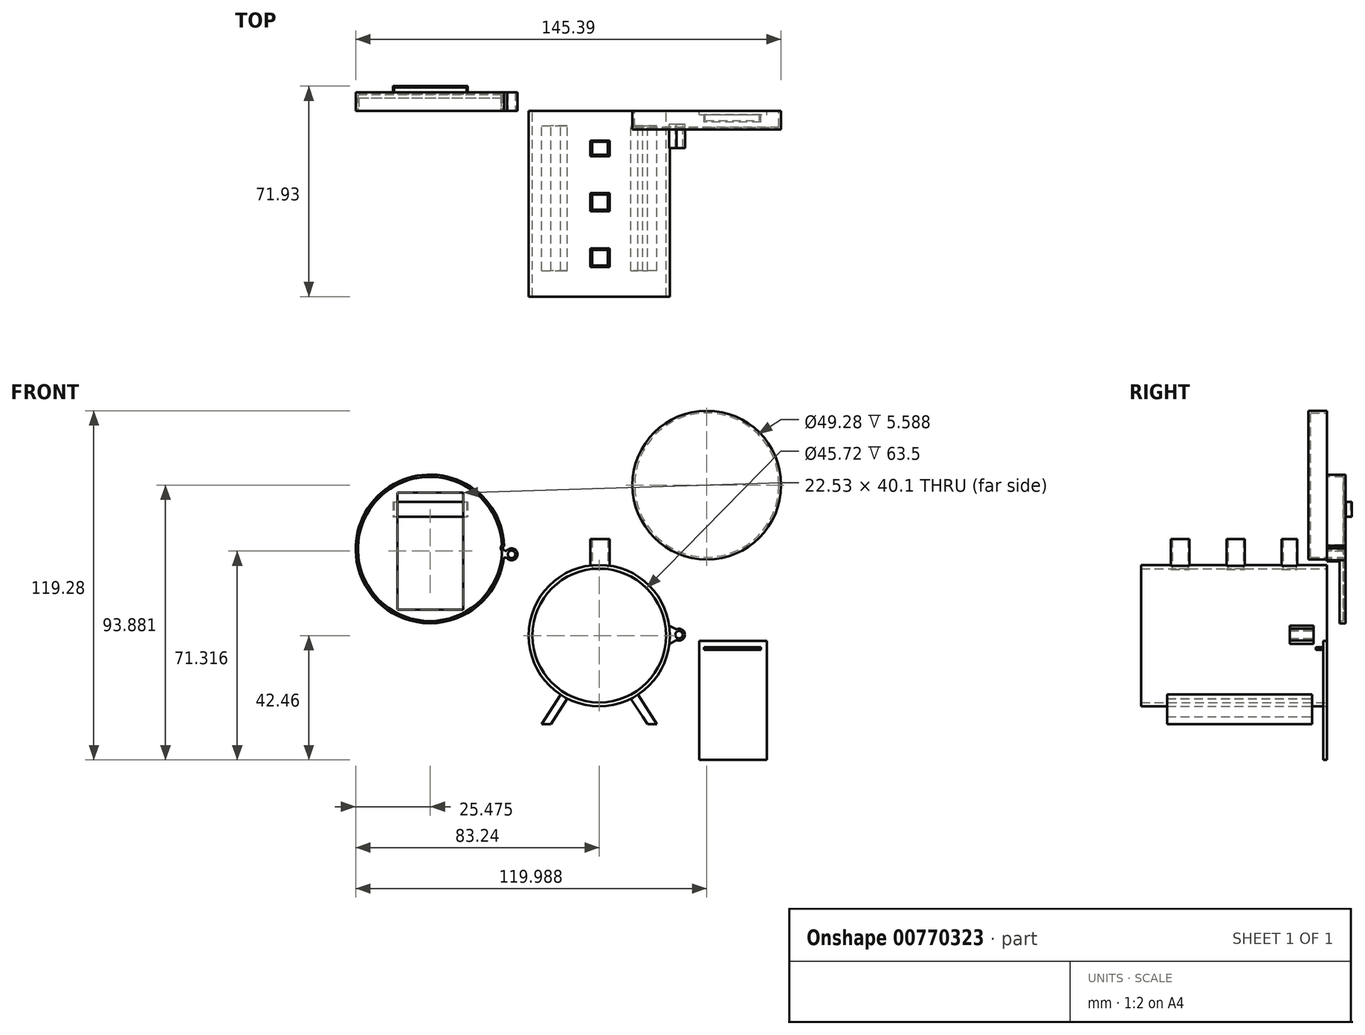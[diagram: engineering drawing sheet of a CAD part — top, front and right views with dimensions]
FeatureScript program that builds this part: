
annotation { "Feature Type Name" : "Feature", "Feature Type Description" : "" }
export const myFeature = defineFeature(function(context is Context, id is Id, definition is map)
    precondition{}
    {
        {
            var Q0;
            Q0=qCreatedBy(makeId("Front.planeOp"),FACE);
            var sketch = newSketch(context, id + "F0", { "sketchPlane" : qUnion([Q0])});
            skCircle(sketch, "E0", {"center": v(-57.84, 29.6) * mm, "radius": 25.4 * mm});
            skCircle(sketch, "E1", {"center": v(36.75, 51.42) * mm, "radius": 25.4 * mm});
            skCircle(sketch, "E2", {"center": v(0, 0) * mm, "radius": 24.13 * mm});
            skCircle(sketch, "E3", {"center": v(0, 0) * mm, "radius": 22.86 * mm});
            skCircle(sketch, "E4", {"center": v(-29.97, 27.74) * mm, "radius": 2.03 * mm});
            skCircle(sketch, "E5", {"center": v(-29.97, 27.74) * mm, "radius": 1.27 * mm});
            skPoint(sketch, "E6", {"position": v(-82.6, 23.93) * mm});
            skArc(sketch, "E7", {"start": v(-31.32, 26.22) * mm, "mid": v(-31.92, 26.64) * mm, "end": v(-32.63, 26.47) * mm});
            skArc(sketch, "E8", {"start": v(-32.46, 30.66) * mm, "mid": v(-32.74, 29.38) * mm, "end": v(-31.47, 29.1) * mm});
            skCircle(sketch, "E9", {"center": v(27.24, 0.29) * mm, "radius": 2.03 * mm});
            skCircle(sketch, "E10", {"center": v(27.24, 0.29) * mm, "radius": 1.27 * mm});
            skLineSegment(sketch, "E11", {"start": v(26.39, 2.13) * mm, "end": v(23.9, 3.39) * mm});
            skLineSegment(sketch, "E12", {"start": v(26.41, -1.57) * mm, "end": v(23.96, -2.9) * mm});
            skLineSegment(sketch, "E13", {"start": v(-19.67, -30.34) * mm, "end": v(-13.17, -20.22) * mm});
            skLineSegment(sketch, "E14", {"start": v(19.68, -30.34) * mm, "end": v(13.24, -20.17) * mm});
            skLineSegment(sketch, "E15", {"start": v(-14.86, -27.7) * mm, "end": v(-10.97, -21.5) * mm});
            skLineSegment(sketch, "E16", {"start": v(14.87, -27.7) * mm, "end": v(10.75, -21.6) * mm});
            skLineSegment(sketch, "E17", {"start": v(14.87, -27.7) * mm, "end": v(16.46, -30.34) * mm});
            skLineSegment(sketch, "E18", {"start": v(19.68, -30.34) * mm, "end": v(16.46, -30.34) * mm});
            skLineSegment(sketch, "E19", {"start": v(-14.86, -27.7) * mm, "end": v(-16.51, -30.34) * mm});
            skLineSegment(sketch, "E20", {"start": v(-19.67, -30.34) * mm, "end": v(-16.51, -30.34) * mm});
            skSolve(sketch);
        }
        {
            var Q0;
            Q0=qCreatedBy(makeId("Top.planeOp"),FACE);
            var sketch = newSketch(context, id + "F1", { "sketchPlane" : qUnion([Q0])});
            skLineSegment(sketch, "E21.bottom", {"start": v(-84.43, -2.05) * mm, "end": v(-31.1, -2.05) * mm});
            skLineSegment(sketch, "E21.top", {"start": v(-84.43, 4.3) * mm, "end": v(-31.1, 4.3) * mm});
            skLineSegment(sketch, "E21.left", {"start": v(-84.43, -2.05) * mm, "end": v(-84.43, 4.3) * mm});
            skLineSegment(sketch, "E21.right", {"start": v(-31.1, -2.05) * mm, "end": v(-31.1, 4.3) * mm});
            skLineSegment(sketch, "E22", {"start": v(-70.15, 8.43) * mm, "end": v(-45.37, 8.43) * mm});
            skLineSegment(sketch, "E23", {"start": v(-70.15, 8) * mm, "end": v(-45.37, 8) * mm});
            skLineSegment(sketch, "E24.bottom", {"start": v(-70.15, 8.43) * mm, "end": v(-70.53, 8.43) * mm});
            skLineSegment(sketch, "E24.right", {"start": v(-70.53, 8.43) * mm, "end": v(-70.53, 6.4) * mm});
            skLineSegment(sketch, "E25", {"start": v(-45.37, 6.4) * mm, "end": v(-45.37, 8) * mm});
            skLineSegment(sketch, "E26", {"start": v(-44.98, 6.4) * mm, "end": v(-44.98, 8.43) * mm});
            skLineSegment(sketch, "E27", {"start": v(-44.98, 8.43) * mm, "end": v(-45.37, 8.43) * mm});
            skLineSegment(sketch, "E28", {"start": v(-70.15, 8) * mm, "end": v(-70.15, 6.4) * mm});
            skLineSegment(sketch, "E29", {"start": v(-70.53, 6.4) * mm, "end": v(-70.15, 6.4) * mm});
            skLineSegment(sketch, "E30", {"start": v(-45.37, 6.4) * mm, "end": v(-44.98, 6.4) * mm});
            skSolve(sketch);
        }
        {
            var Q0;
            Q0=qCreatedBy(makeId("Front.planeOp"),FACE);
            var sketch = newSketch(context, id + "F2", { "sketchPlane" : qUnion([Q0])});
            skLineSegment(sketch, "E31.bottom", {"start": v(-46.5, 48.9) * mm, "end": v(-69.03, 48.9) * mm});
            skLineSegment(sketch, "E31.top", {"start": v(-46.5, 8.8) * mm, "end": v(-69.03, 8.8) * mm});
            skLineSegment(sketch, "E31.left", {"start": v(-46.5, 48.9) * mm, "end": v(-46.5, 8.8) * mm});
            skLineSegment(sketch, "E31.right", {"start": v(-69.03, 48.9) * mm, "end": v(-69.03, 8.8) * mm});
            skLineSegment(sketch, "E32.bottom", {"start": v(34.2, -42.46) * mm, "end": v(57.24, -42.46) * mm});
            skLineSegment(sketch, "E32.top", {"start": v(34.2, -1.82) * mm, "end": v(57.24, -1.82) * mm});
            skLineSegment(sketch, "E32.left", {"start": v(34.2, -42.46) * mm, "end": v(34.2, -1.82) * mm});
            skLineSegment(sketch, "E32.right", {"start": v(57.24, -42.46) * mm, "end": v(57.24, -1.82) * mm});
            skLineSegment(sketch, "E33.bottom", {"start": v(55.19, -3.96) * mm, "end": v(35.8, -3.96) * mm});
            skLineSegment(sketch, "E33.top", {"start": v(55.19, -4.91) * mm, "end": v(35.8, -4.91) * mm});
            skLineSegment(sketch, "E33.left", {"start": v(55.19, -3.96) * mm, "end": v(55.19, -4.91) * mm});
            skLineSegment(sketch, "E33.right", {"start": v(35.8, -3.96) * mm, "end": v(35.8, -4.91) * mm});
            skSolve(sketch);
        }
        {
            var Q0;
            Q0=makeQuery(id+"F0.imprint","IMPRINT",FACE,{"disambiguationData":[TD([[makeQuery(id+"F0.imprint","IMPRINT",EDGE,{"derivedFrom":sQuery(id+"F0.wireOp",EDGE,"E0")}),1.0]])]});
            var Q1;
            Q1=makeQuery(id+"F0.imprint","IMPRINT",FACE,{"disambiguationData":[TD([[makeQuery(id+"F0.imprint","IMPRINT",EDGE,{"derivedFrom":sQuery(id+"F0.wireOp",EDGE,"C6JpCIsN-Ug02-e6we-Fdyt-q6CA1btcc4Vs")}),1.0]])]});
            var Q2;
            Q2=sQuery(id+"F0.wireOp",EDGE,"E0");
            extrude(context, id + "F3", {"entities" : qUnion([Q0, Q1]), "surfaceEntities" : qUnion([Q2]), "oppositeDirection" : true, "depth" : 6.35 * mm, "offsetDistance" : 25.4 * mm});
        }
        {
            var Q0;
            Q0=makeQuery(id+"F0.imprint","IMPRINT",FACE,{"disambiguationData":[TD([[makeQuery(id+"F0.imprint","IMPRINT",EDGE,{"derivedFrom":sQuery(id+"F0.wireOp",EDGE,"E1")}),1.0]])]});
            var Q1;
            Q1=sQuery(id+"F0.wireOp",EDGE,"E1");
            extrude(context, id + "F4", {"entities" : qUnion([Q0]), "surfaceEntities" : qUnion([Q1]), "depth" : 6.35 * mm, "offsetDistance" : 25.4 * mm});
        }
        {
            var Q0;
            Q0=makeQuery(id+"F0.imprint","IMPRINT",FACE,{"disambiguationData":[TD([[makeQuery(id+"F0.imprint","IMPRINT",EDGE,{"derivedFrom":sQuery(id+"F0.wireOp",EDGE,"E2")}),1.0]])]});
            var Q1;
            Q1=sQuery(id+"F0.wireOp",EDGE,"E2");
            extrude(context, id + "F5", {"entities" : qUnion([Q0]), "surfaceEntities" : qUnion([Q1]), "depth" : 63.5 * mm, "offsetDistance" : 25.4 * mm});
        }
        {
            var Q0;
            Q0=makeQuery(id+"F0.imprint","IMPRINT",FACE,{"disambiguationData":[TD([[makeQuery(id+"F0.imprint","IMPRINT",EDGE,{"derivedFrom":sQuery(id+"F0.wireOp",EDGE,"E9")}),1.0]])]});
            var Q1;
            {var subQ0=sQuery(id+"F0.wireOp",EDGE,"4RHoPJRj-vLUF-sawJ-OMLI-LrxcrPkEBD53");Q1=makeQuery(id+"F0.imprint","IMPRINT",FACE,{"disambiguationData":[TD([[makeQuery(id+"F0.imprint","IMPRINT",EDGE,{"derivedFrom":subQ0}),-1.0]])]});}
            var Q2;
            {var subQ0=sQuery(id+"F0.wireOp",EDGE,"GAmkWysi-UypD-Y6Y5-O07L-UFwPJowarkKv");Q2=makeQuery(id+"F0.imprint","IMPRINT",FACE,{"disambiguationData":[TD([[makeQuery(id+"F0.imprint","IMPRINT",EDGE,{"derivedFrom":subQ0}),-1.0]])]});}
            var Q3;
            {var subQ0=sQuery(id+"F0.wireOp",EDGE,"E11");Q3=makeQuery(id+"F0.imprint","IMPRINT",FACE,{"disambiguationData":[TD([[makeQuery(id+"F0.imprint","IMPRINT",EDGE,{"derivedFrom":subQ0}),1.0]])]});}
            extrude(context, id + "F6", {"entities" : qUnion([Q0, Q1, Q2, Q3]), "depth" : 12.7 * mm, "offsetDistance" : 25.4 * mm});
        }
        {
            var Q0;
            Q0=makeQuery(id+"F3.opExtrude","CAP_FACE",FACE,{"disambiguationData":[OSD([sQuery(id+"F0.wireOp",EDGE,"E0")])],"isStart":true});
            shell(context, id + "F7", {"entities" : qUnion([Q0]), "thickness" : 0.76 * mm});
        }
        {
            var Q0;
            Q0=makeQuery(id+"F1.imprint","IMPRINT",FACE,{"disambiguationData":[TD([[makeQuery(id+"F1.imprint","IMPRINT",EDGE,{"derivedFrom":sQuery(id+"F1.wireOp",EDGE,"E21.bottom")}),1.0]])]});
            extrude(context, id + "F8", {"entities" : qUnion([Q0]), "operationType" : NewBodyOperationType.REMOVE, "depth" : 25.4 * mm, "offsetDistance" : 25.4 * mm});
        }
        {
            var Q0;
            {var subQ0=sQuery(id+"F0.wireOp",EDGE,"E7");var subQ1=sQuery(id+"F0.wireOp",EDGE,"E0");var subQ2=makeQuery(id+"F0.imprint","INTERSECT",VERTEX,{"derivedFrom":[subQ1,subQ0]});Q0=makeQuery(id+"F0.imprint","IMPRINT",FACE,{"disambiguationData":[TD([[makeQuery(id+"F0.imprint","IMPRINT",EDGE,{"disambiguationData":[TD([[subQ2,-1.0]])],"derivedFrom":subQ1}),-1.0]])]});}
            var Q1;
            Q1=makeQuery(id+"F0.imprint","IMPRINT",FACE,{"disambiguationData":[TD([[makeQuery(id+"F0.imprint","IMPRINT",EDGE,{"derivedFrom":sQuery(id+"F0.wireOp",EDGE,"E5")}),-1.0]])]});
            var Q2;
            Q2=sQuery(id+"F0.wireOp",EDGE,"E4");
            var Q3;
            Q3=sQuery(id+"F0.wireOp",EDGE,"uoLiYAiw-HX8z-VXfl-kdci-X3IbJ3UhpFK8");
            extrude(context, id + "F9", {"entities" : qUnion([Q0, Q1]), "operationType" : NewBodyOperationType.ADD, "surfaceEntities" : qUnion([Q2, Q3]), "oppositeDirection" : true, "depth" : 6.35 * mm, "offsetDistance" : 25.4 * mm});
        }
        {
            var Q0;
            Q0=makeQuery(id+"F4.opExtrude","CAP_FACE",FACE,{"disambiguationData":[OSD([sQuery(id+"F0.wireOp",EDGE,"E1")])],"isStart":true});
            shell(context, id + "F10", {"entities" : qUnion([Q0]), "thickness" : 0.76 * mm});
        }
        {
            var Q0;
            Q0=makeQuery(id+"F2.imprint","IMPRINT",FACE,{"disambiguationData":[TD([[makeQuery(id+"F2.imprint","IMPRINT",EDGE,{"derivedFrom":sQuery(id+"F2.wireOp",EDGE,"E31.bottom")}),1.0]])]});
            extrude(context, id + "F11", {"entities" : qUnion([Q0]), "operationType" : NewBodyOperationType.REMOVE, "surfaceOperationType" : NewSurfaceOperationType.ADD, "oppositeDirection" : true, "depth" : 12.7 * mm, "offsetDistance" : 25.4 * mm});
        }
        {
            var Q0;
            Q0=makeQuery(id+"F0.imprint","IMPRINT",FACE,{"disambiguationData":[TD([[makeQuery(id+"F0.imprint","IMPRINT",EDGE,{"derivedFrom":sQuery(id+"F0.wireOp",EDGE,"E10")}),-1.0]])]});
            var Q1;
            {var subQ0=sQuery(id+"F0.wireOp",EDGE,"E11");Q1=makeQuery(id+"F0.imprint","IMPRINT",FACE,{"disambiguationData":[TD([[makeQuery(id+"F0.imprint","IMPRINT",EDGE,{"derivedFrom":subQ0}),1.0]])]});}
            extrude(context, id + "F12", {"entities" : qUnion([Q0, Q1]), "operationType" : NewBodyOperationType.REMOVE, "depth" : 4.57 * mm, "offsetDistance" : 25.4 * mm});
        }
        {
            var Q0;
            Q0=makeQuery(id+"F1.imprint","IMPRINT",FACE,{"disambiguationData":[TD([[makeQuery(id+"F1.imprint","IMPRINT",EDGE,{"derivedFrom":sQuery(id+"F1.wireOp",EDGE,"E22")}),-1.0]])]});
            var Q1;
            Q1=sQuery(id+"F1.wireOp",EDGE,"E23");
            var Q2;
            Q2=sQuery(id+"F1.wireOp",EDGE,"E22");
            var Q3;
            Q3=sQuery(id+"F1.wireOp",EDGE,"E24.right");
            var Q4;
            Q4=sQuery(id+"F1.wireOp",EDGE,"E28");
            var Q5;
            Q5=sQuery(id+"F1.wireOp",EDGE,"E26");
            var Q6;
            Q6=sQuery(id+"F1.wireOp",EDGE,"E25");
            var Q7;
            Q7=sQuery(id+"F1.wireOp",EDGE,"E27");
            var Q8;
            Q8=sQuery(id+"F1.wireOp",EDGE,"E24.top");
            var Q9;
            Q9=sQuery(id+"F1.wireOp",EDGE,"XSHV3Paq-2D3R-pDyN-Gvgj-U2klOx5jiF1c");
            var Q10;
            Q10=sQuery(id+"F1.wireOp",EDGE,"E24.bottom");
            extrude(context, id + "F13", {"entities" : qUnion([Q0]), "operationType" : NewBodyOperationType.ADD, "surfaceEntities" : qUnion([Q1, Q2, Q3, Q4, Q5, Q6, Q7, Q8, Q9, Q10]), "depth" : 45.72 * mm, "offsetDistance" : 25.4 * mm});
        }
        {
            var Q0;
            Q0=makeQuery(id+"F1.imprint","IMPRINT",FACE,{"disambiguationData":[TD([[makeQuery(id+"F1.imprint","IMPRINT",EDGE,{"derivedFrom":sQuery(id+"F1.wireOp",EDGE,"E22")}),-1.0]])]});
            var Q1;
            Q1=sQuery(id+"F1.wireOp",EDGE,"E28");
            var Q2;
            Q2=sQuery(id+"F1.wireOp",EDGE,"E23");
            var Q3;
            Q3=sQuery(id+"F1.wireOp",EDGE,"E25");
            var Q4;
            Q4=sQuery(id+"F1.wireOp",EDGE,"E26");
            var Q5;
            Q5=sQuery(id+"F1.wireOp",EDGE,"E24.right");
            var Q6;
            Q6=sQuery(id+"F1.wireOp",EDGE,"E22");
            var Q7;
            Q7=sQuery(id+"F1.wireOp",EDGE,"E27");
            var Q8;
            Q8=sQuery(id+"F1.wireOp",EDGE,"E24.top");
            var Q9;
            Q9=sQuery(id+"F1.wireOp",EDGE,"XSHV3Paq-2D3R-pDyN-Gvgj-U2klOx5jiF1c");
            var Q10;
            Q10=sQuery(id+"F1.wireOp",EDGE,"E24.bottom");
            extrude(context, id + "F14", {"entities" : qUnion([Q0]), "operationType" : NewBodyOperationType.REMOVE, "surfaceEntities" : qUnion([Q1, Q2, Q3, Q4, Q5, Q6, Q7, Q8, Q9, Q10]), "depth" : 40.64 * mm, "offsetDistance" : 25.4 * mm});
        }
        {
            var Q0;
            Q0=makeQuery(id+"F2.imprint","IMPRINT",FACE,{"disambiguationData":[TD([[makeQuery(id+"F2.imprint","IMPRINT",EDGE,{"derivedFrom":sQuery(id+"F2.wireOp",EDGE,"E32.bottom")}),1.0]])]});
            extrude(context, id + "F15", {"entities" : qUnion([Q0]), "depth" : 1.27 * mm, "offsetDistance" : 25.4 * mm});
        }
        {
            var Q0;
            Q0=qCreatedBy(makeId("Top.planeOp"),FACE);
            var sketch = newSketch(context, id + "F16", { "sketchPlane" : qUnion([Q0])});
            skLineSegment(sketch, "E34.bottom", {"start": v(-3, -10.16) * mm, "end": v(3.54, -10.16) * mm});
            skLineSegment(sketch, "E34.top", {"start": v(-3, -15.53) * mm, "end": v(3.54, -15.53) * mm});
            skLineSegment(sketch, "E34.left", {"start": v(-3, -10.16) * mm, "end": v(-3, -15.53) * mm});
            skLineSegment(sketch, "E34.right", {"start": v(3.54, -10.16) * mm, "end": v(3.54, -15.53) * mm});
            skLineSegment(sketch, "E35.bottom", {"start": v(-3, -28.07) * mm, "end": v(3.54, -28.07) * mm});
            skLineSegment(sketch, "E35.top", {"start": v(-3, -34.35) * mm, "end": v(3.54, -34.35) * mm});
            skLineSegment(sketch, "E35.left", {"start": v(-3, -28.07) * mm, "end": v(-3, -34.35) * mm});
            skLineSegment(sketch, "E35.right", {"start": v(3.54, -28.07) * mm, "end": v(3.54, -34.35) * mm});
            skLineSegment(sketch, "E36.bottom", {"start": v(-3, -47.05) * mm, "end": v(3.54, -47.05) * mm});
            skLineSegment(sketch, "E36.top", {"start": v(-3, -53.34) * mm, "end": v(3.54, -53.34) * mm});
            skLineSegment(sketch, "E36.left", {"start": v(-3, -47.05) * mm, "end": v(-3, -53.34) * mm});
            skLineSegment(sketch, "E36.right", {"start": v(3.54, -47.05) * mm, "end": v(3.54, -53.34) * mm});
            skLineSegment(sketch, "E37.bottom", {"start": v(-2.43, -10.6) * mm, "end": v(2.96, -10.6) * mm});
            skLineSegment(sketch, "E37.top", {"start": v(-2.43, -14.99) * mm, "end": v(2.96, -14.99) * mm});
            skLineSegment(sketch, "E37.left", {"start": v(-2.43, -10.6) * mm, "end": v(-2.43, -14.99) * mm});
            skLineSegment(sketch, "E37.right", {"start": v(2.96, -10.6) * mm, "end": v(2.96, -14.99) * mm});
            skLineSegment(sketch, "E38.bottom", {"start": v(-2.44, -28.57) * mm, "end": v(2.96, -28.57) * mm});
            skLineSegment(sketch, "E38.top", {"start": v(-2.44, -33.77) * mm, "end": v(2.96, -33.77) * mm});
            skLineSegment(sketch, "E38.left", {"start": v(-2.44, -28.57) * mm, "end": v(-2.44, -33.77) * mm});
            skLineSegment(sketch, "E38.right", {"start": v(2.96, -28.57) * mm, "end": v(2.96, -33.77) * mm});
            skLineSegment(sketch, "E39.bottom", {"start": v(-2.44, -47.57) * mm, "end": v(2.96, -47.57) * mm});
            skLineSegment(sketch, "E39.top", {"start": v(-2.44, -52.83) * mm, "end": v(2.96, -52.83) * mm});
            skLineSegment(sketch, "E39.left", {"start": v(-2.44, -47.57) * mm, "end": v(-2.44, -52.83) * mm});
            skLineSegment(sketch, "E39.right", {"start": v(2.96, -47.57) * mm, "end": v(2.96, -52.83) * mm});
            skSolve(sketch);
        }
        {
            var Q0;
            Q0 = qSketchRegion(id + "F16", true);
            extrude(context, id + "F17", {"entities" : qUnion([Q0]), "operationType" : NewBodyOperationType.ADD, "depth" : 33.02 * mm, "offsetDistance" : 25.4 * mm});
        }
        {
            var Q0;
            Q0=makeQuery(id+"F16.imprint","IMPRINT",FACE,{"disambiguationData":[TD([[makeQuery(id+"F16.imprint","IMPRINT",EDGE,{"derivedFrom":sQuery(id+"F16.wireOp",EDGE,"E35.bottom")}),-1.0]])]});
            var Q1;
            Q1=makeQuery(id+"F16.imprint","IMPRINT",FACE,{"disambiguationData":[TD([[makeQuery(id+"F16.imprint","IMPRINT",EDGE,{"derivedFrom":sQuery(id+"F16.wireOp",EDGE,"E34.bottom")}),-1.0]])]});
            var Q2;
            Q2=makeQuery(id+"F16.imprint","IMPRINT",FACE,{"disambiguationData":[TD([[makeQuery(id+"F16.imprint","IMPRINT",EDGE,{"derivedFrom":sQuery(id+"F16.wireOp",EDGE,"E36.bottom")}),-1.0]])]});
            extrude(context, id + "F18", {"entities" : qUnion([Q0, Q1, Q2]), "operationType" : NewBodyOperationType.REMOVE, "depth" : 22.86 * mm, "offsetDistance" : 25.4 * mm});
        }
        {
            var Q0;
            Q0=makeQuery(id+"F16.imprint","IMPRINT",FACE,{"disambiguationData":[TD([[makeQuery(id+"F16.imprint","IMPRINT",EDGE,{"derivedFrom":sQuery(id+"F16.wireOp",EDGE,"E37.bottom")}),-1.0]])]});
            var Q1;
            Q1=makeQuery(id+"F16.imprint","IMPRINT",FACE,{"disambiguationData":[TD([[makeQuery(id+"F16.imprint","IMPRINT",EDGE,{"derivedFrom":sQuery(id+"F16.wireOp",EDGE,"E38.bottom")}),-1.0]])]});
            var Q2;
            Q2=makeQuery(id+"F16.imprint","IMPRINT",FACE,{"disambiguationData":[TD([[makeQuery(id+"F16.imprint","IMPRINT",EDGE,{"derivedFrom":sQuery(id+"F16.wireOp",EDGE,"E39.bottom")}),-1.0]])]});
            var Q3;
            Q3=sQuery(id+"F16.wireOp",EDGE,"E37.left");
            var Q4;
            Q4=sQuery(id+"F16.wireOp",EDGE,"E37.right");
            var Q5;
            Q5=sQuery(id+"F16.wireOp",EDGE,"E37.bottom");
            var Q6;
            Q6=sQuery(id+"F16.wireOp",EDGE,"E37.top");
            var Q7;
            Q7=sQuery(id+"F16.wireOp",EDGE,"E38.bottom");
            var Q8;
            Q8=sQuery(id+"F16.wireOp",EDGE,"E38.top");
            var Q9;
            Q9=sQuery(id+"F16.wireOp",EDGE,"E38.left");
            var Q10;
            Q10=sQuery(id+"F16.wireOp",EDGE,"E38.right");
            var Q11;
            Q11=sQuery(id+"F16.wireOp",EDGE,"E39.left");
            var Q12;
            Q12=sQuery(id+"F16.wireOp",EDGE,"E39.top");
            var Q13;
            Q13=sQuery(id+"F16.wireOp",EDGE,"E39.right");
            var Q14;
            Q14=sQuery(id+"F16.wireOp",EDGE,"E39.bottom");
            extrude(context, id + "F19", {"entities" : qUnion([Q0, Q1, Q2]), "operationType" : NewBodyOperationType.REMOVE, "surfaceEntities" : qUnion([Q3, Q4, Q5, Q6, Q7, Q8, Q9, Q10, Q11, Q12, Q13, Q14]), "endBound" : BoundingType.THROUGH_ALL, "depth" : 25.4 * mm, "offsetDistance" : 25.4 * mm});
        }
        {
            var Q0;
            Q0=makeQuery(id+"F2.imprint","IMPRINT",FACE,{"disambiguationData":[TD([[makeQuery(id+"F2.imprint","IMPRINT",EDGE,{"derivedFrom":sQuery(id+"F2.wireOp",EDGE,"E33.bottom")}),1.0]])]});
            extrude(context, id + "F20", {"entities" : qUnion([Q0]), "operationType" : NewBodyOperationType.ADD, "depth" : 3.8 * mm, "offsetDistance" : 25.4 * mm});
        }
        {
            var Q0;
            Q0=qCreatedBy(makeId("Top.planeOp"),FACE);
            var sketch = newSketch(context, id + "F21", { "sketchPlane" : qUnion([Q0])});
            skLineSegment(sketch, "E40.bottom", {"start": v(36.21, -3.36) * mm, "end": v(54.76, -3.36) * mm});
            skLineSegment(sketch, "E40.top", {"start": v(36.21, -1.37) * mm, "end": v(54.76, -1.37) * mm});
            skLineSegment(sketch, "E40.left", {"start": v(36.21, -3.36) * mm, "end": v(36.21, -1.37) * mm});
            skLineSegment(sketch, "E40.right", {"start": v(54.76, -3.36) * mm, "end": v(54.76, -1.37) * mm});
            skSolve(sketch);
        }
        {
            var Q0;
            Q0 = qSketchRegion(id + "F21", true);
            extrude(context, id + "F22", {"entities" : qUnion([Q0]), "operationType" : NewBodyOperationType.REMOVE, "endBound" : BoundingType.SYMMETRIC, "depth" : 12.7 * mm, "offsetDistance" : 25.4 * mm});
        }
        {
            var Q0;
            {var subQ0=sQuery(id+"F0.wireOp",EDGE,"E14");Q0=makeQuery(id+"F0.imprint","IMPRINT",FACE,{"disambiguationData":[TD([[makeQuery(id+"F0.imprint","IMPRINT",EDGE,{"derivedFrom":subQ0}),1.0]])]});}
            var Q1;
            {var subQ1=sQuery(id+"F0.wireOp",EDGE,"E13");Q1=makeQuery(id+"F0.imprint","IMPRINT",FACE,{"disambiguationData":[TD([[makeQuery(id+"F0.imprint","IMPRINT",EDGE,{"derivedFrom":subQ1}),-1.0]])]});}
            extrude(context, id + "F23", {"entities" : qUnion([Q0, Q1]), "operationType" : NewBodyOperationType.ADD, "depth" : 54.6 * mm, "offsetDistance" : 25.4 * mm});
        }
        {
            var Q0;
            {var subQ0=sQuery(id+"F0.wireOp",EDGE,"E14");Q0=makeQuery(id+"F0.imprint","IMPRINT",FACE,{"disambiguationData":[TD([[makeQuery(id+"F0.imprint","IMPRINT",EDGE,{"derivedFrom":subQ0}),1.0]])]});}
            var Q1;
            {var subQ1=sQuery(id+"F0.wireOp",EDGE,"E13");Q1=makeQuery(id+"F0.imprint","IMPRINT",FACE,{"disambiguationData":[TD([[makeQuery(id+"F0.imprint","IMPRINT",EDGE,{"derivedFrom":subQ1}),-1.0]])]});}
            extrude(context, id + "F24", {"entities" : qUnion([Q0, Q1]), "operationType" : NewBodyOperationType.REMOVE, "depth" : 5.08 * mm, "offsetDistance" : 25.4 * mm});
        }
    });
